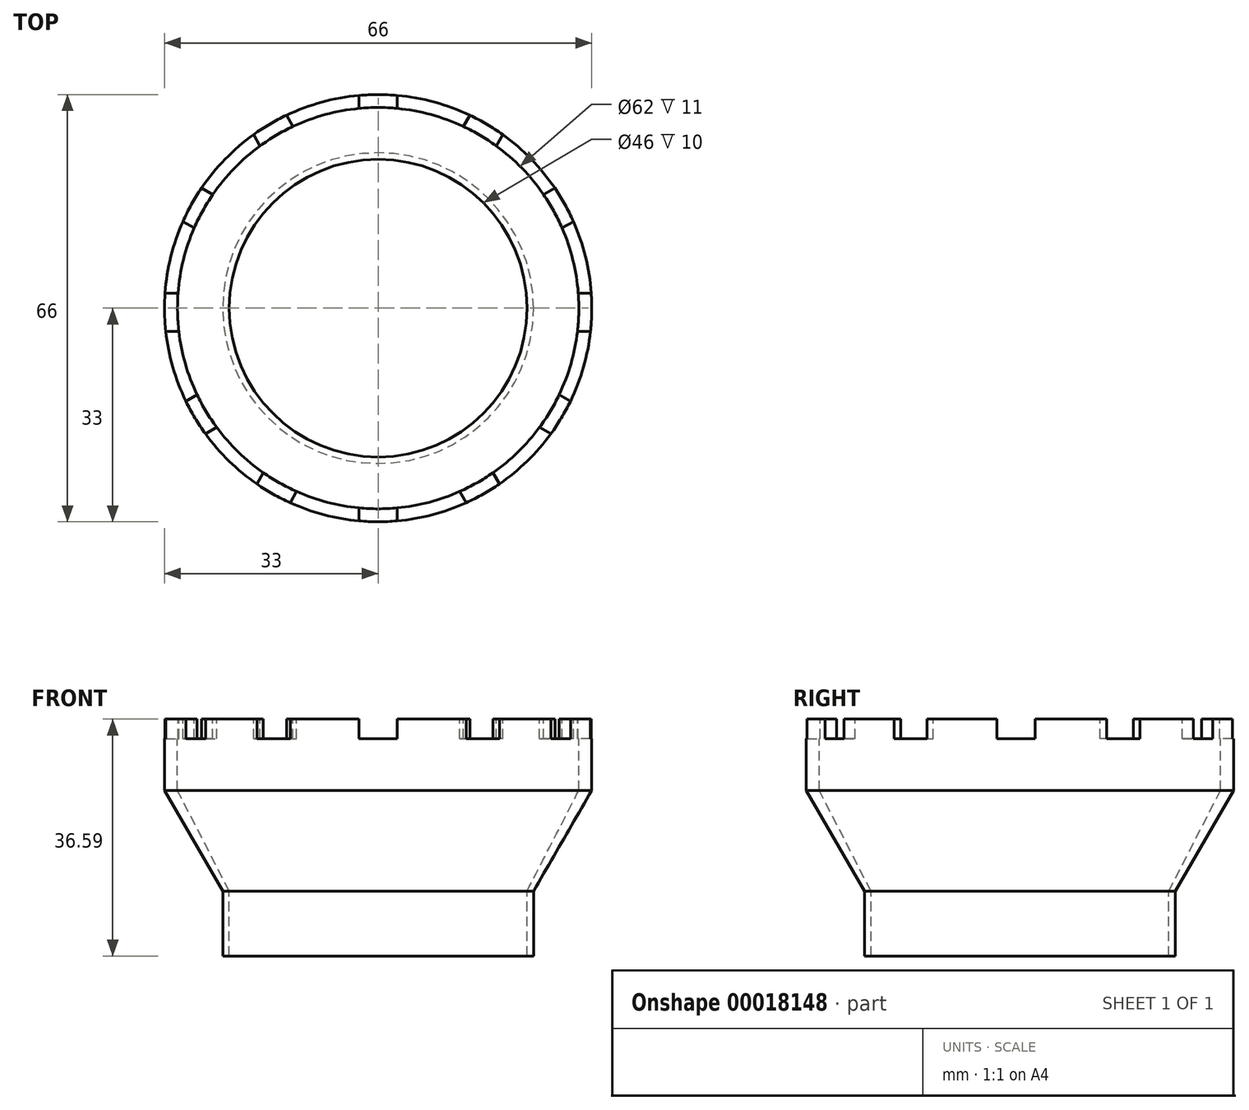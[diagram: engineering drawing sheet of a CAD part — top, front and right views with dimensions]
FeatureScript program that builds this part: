
annotation { "Feature Type Name" : "Feature", "Feature Type Description" : "" }
export const myFeature = defineFeature(function(context is Context, id is Id, definition is map)
    precondition{}
    {
        {
            var Q0;
            Q0=qCreatedBy(makeId("Top.planeOp"),FACE);
            var sketch = newSketch(context, id + "F0", { "sketchPlane" : qUnion([Q0])});
            skCircle(sketch, "E0", {"center": v(0, 0) * mm, "radius": 24 * mm});
            skSolve(sketch);
        }
        {
            var Q0;
            Q0=makeQuery(id+"F0.imprint","IMPRINT",FACE,{"disambiguationData":[TD([[makeQuery(id+"F0.imprint","IMPRINT",EDGE,{"derivedFrom":sQuery(id+"F0.wireOp",EDGE,"E0")}),1.0]])]});
            extrude(context, id + "F1", {"entities" : qUnion([Q0]), "depth" : 10 * mm});
        }
        {
            var Q0;
            Q0=makeQuery(id+"F1.opExtrude","CAP_FACE",FACE,{"disambiguationData":[OSD([sQuery(id+"F0.wireOp",EDGE,"E0")])],"isStart":false});
            var sketch = newSketch(context, id + "F2", { "sketchPlane" : qUnion([Q0])});
            skCircle(sketch, "E1", {"center": v(0, 0) * mm, "radius": 23 * mm});
            skSolve(sketch);
        }
        {
            var Q0;
            Q0=qSketchRegion(id+"F2",true);
            extrude(context, id + "F3", {"entities" : qUnion([Q0]), "operationType" : NewBodyOperationType.REMOVE, "endBound" : BoundingType.THROUGH_ALL, "oppositeDirection" : true, "depth" : 25 * mm});
        }
        {
            var Q0;
            Q0=qCreatedBy(makeId("Front.planeOp"),FACE);
            var sketch = newSketch(context, id + "F4", { "sketchPlane" : qUnion([Q0])});
            skLineSegment(sketch, "E2", {"start": v(-31, 25.59) * mm, "end": v(-31, 36.59) * mm});
            skLineSegment(sketch, "E3", {"start": v(-31, 36.59) * mm, "end": v(-33, 36.59) * mm});
            skLineSegment(sketch, "E4", {"start": v(-33, 36.59) * mm, "end": v(-33, 25.59) * mm});
            skLineSegment(sketch, "E5", {"start": v(-33, 25.59) * mm, "end": v(-24, 10) * mm});
            skLineSegment(sketch, "E6", {"start": v(-24, 10) * mm, "end": v(-23, 10) * mm});
            skLineSegment(sketch, "E7", {"start": v(-23, 10) * mm, "end": v(-31, 25.59) * mm});
            skLineSegment(sketch, "E8.0", {"start": v(-24, 10) * mm, "end": v(24, 10) * mm});
            skLineSegment(sketch, "E9", {"start": v(-33, 25.59) * mm, "end": v(-33, 10) * mm, "construction": true});
            skSolve(sketch);
        }
        {
            var Q0;
            Q0=qSketchRegion(id+"F4",true);
            var Q1;
            Q1=makeQuery(id+"F3.boolean.opBoolean","COPY",FACE,{"derivedFrom":makeQuery(id+"F3.opExtrude","SWEPT_FACE",FACE,{"disambiguationData":[OSD([sQuery(id+"F2.wireOp",EDGE,"E1")])]})});
            revolve(context, id + "F5", {"operationType" : NewBodyOperationType.ADD, "entities" : qUnion([Q0]), "axis" : qUnion([Q1]), "revolveType" : RevolveType.FULL});
        }
        {
            var Q0;
            Q0=makeQuery(id+"F5.opRevolve","SWEPT_FACE",FACE,{"disambiguationData":[OSD([sQuery(id+"F4.wireOp",EDGE,"E3")])]});
            var sketch = newSketch(context, id + "F6", { "sketchPlane" : qUnion([Q0])});
            skLineSegment(sketch, "E10.rect.bottom", {"start": v(-2.95, 33.18) * mm, "end": v(2.95, 33.18) * mm});
            skLineSegment(sketch, "E10.rect.top", {"start": v(-2.95, 28.82) * mm, "end": v(2.95, 28.82) * mm});
            skLineSegment(sketch, "E10.rect.left", {"start": v(-2.95, 33.18) * mm, "end": v(-2.95, 28.82) * mm});
            skLineSegment(sketch, "E10.rect.right", {"start": v(2.95, 33.18) * mm, "end": v(2.95, 28.82) * mm});
            skPoint(sketch, "E10.rect.middle", {"position": v(0, 31) * mm});
            skPoint(sketch, "E11.1.2", {"position": v(-15.8, 26.76) * mm});
            skLineSegment(sketch, "E11.1.9", {"start": v(-19.46, 27.18) * mm, "end": v(-14.35, 30.13) * mm});
            skLineSegment(sketch, "E11.1.10", {"start": v(-17.27, 23.4) * mm, "end": v(-12.16, 26.35) * mm});
            skLineSegment(sketch, "E11.1.11", {"start": v(-19.46, 27.18) * mm, "end": v(-17.27, 23.4) * mm});
            skLineSegment(sketch, "E11.1.12", {"start": v(-14.35, 30.13) * mm, "end": v(-12.16, 26.35) * mm});
            skPoint(sketch, "E11.2.2", {"position": v(-27.38, 15.2) * mm});
            skLineSegment(sketch, "E11.2.9", {"start": v(-30.75, 13.73) * mm, "end": v(-27.8, 18.84) * mm});
            skLineSegment(sketch, "E11.2.10", {"start": v(-26.97, 11.54) * mm, "end": v(-24.02, 16.65) * mm});
            skLineSegment(sketch, "E11.2.11", {"start": v(-30.75, 13.73) * mm, "end": v(-26.97, 11.54) * mm});
            skLineSegment(sketch, "E11.2.12", {"start": v(-27.8, 18.84) * mm, "end": v(-24.02, 16.65) * mm});
            skPoint(sketch, "E11.3.2", {"position": v(-31.62, -0.62) * mm});
            skLineSegment(sketch, "E11.3.9", {"start": v(-33.8, -3.57) * mm, "end": v(-33.8, 2.33) * mm});
            skLineSegment(sketch, "E11.3.10", {"start": v(-29.43, -3.57) * mm, "end": v(-29.43, 2.33) * mm});
            skLineSegment(sketch, "E11.3.11", {"start": v(-33.8, -3.57) * mm, "end": v(-29.43, -3.57) * mm});
            skLineSegment(sketch, "E11.3.12", {"start": v(-33.8, 2.33) * mm, "end": v(-29.43, 2.33) * mm});
            skPoint(sketch, "E11.4.2", {"position": v(-27.38, -16.43) * mm});
            skLineSegment(sketch, "E11.4.9", {"start": v(-27.8, -20.07) * mm, "end": v(-30.75, -14.97) * mm});
            skLineSegment(sketch, "E11.4.10", {"start": v(-24.02, -17.89) * mm, "end": v(-26.97, -12.78) * mm});
            skLineSegment(sketch, "E11.4.11", {"start": v(-27.8, -20.07) * mm, "end": v(-24.02, -17.89) * mm});
            skLineSegment(sketch, "E11.4.12", {"start": v(-30.75, -14.97) * mm, "end": v(-26.97, -12.78) * mm});
            skPoint(sketch, "E11.5.2", {"position": v(-15.8, -28) * mm});
            skLineSegment(sketch, "E11.5.9", {"start": v(-14.35, -31.37) * mm, "end": v(-19.46, -28.42) * mm});
            skLineSegment(sketch, "E11.5.10", {"start": v(-12.16, -27.58) * mm, "end": v(-17.27, -24.63) * mm});
            skLineSegment(sketch, "E11.5.11", {"start": v(-14.35, -31.37) * mm, "end": v(-12.16, -27.58) * mm});
            skLineSegment(sketch, "E11.5.12", {"start": v(-19.46, -28.42) * mm, "end": v(-17.27, -24.63) * mm});
            skPoint(sketch, "E11.6.2", {"position": v(0, -32.24) * mm});
            skLineSegment(sketch, "E11.6.9", {"start": v(2.95, -34.42) * mm, "end": v(-2.95, -34.42) * mm});
            skLineSegment(sketch, "E11.6.10", {"start": v(2.95, -30.05) * mm, "end": v(-2.95, -30.05) * mm});
            skLineSegment(sketch, "E11.6.11", {"start": v(2.95, -34.42) * mm, "end": v(2.95, -30.05) * mm});
            skLineSegment(sketch, "E11.6.12", {"start": v(-2.95, -34.42) * mm, "end": v(-2.95, -30.05) * mm});
            skPoint(sketch, "E11.7.2", {"position": v(15.8, -28) * mm});
            skLineSegment(sketch, "E11.7.9", {"start": v(19.46, -28.42) * mm, "end": v(14.35, -31.37) * mm});
            skLineSegment(sketch, "E11.7.10", {"start": v(17.27, -24.63) * mm, "end": v(12.16, -27.58) * mm});
            skLineSegment(sketch, "E11.7.11", {"start": v(19.46, -28.42) * mm, "end": v(17.27, -24.63) * mm});
            skLineSegment(sketch, "E11.7.12", {"start": v(14.35, -31.37) * mm, "end": v(12.16, -27.58) * mm});
            skPoint(sketch, "E11.center", {"position": v(0, -0.62) * mm});
            skPoint(sketch, "E12.2.8.0", {"position": v(27.38, -16.43) * mm});
            skLineSegment(sketch, "E12.9.8.0", {"start": v(30.75, -14.97) * mm, "end": v(27.8, -20.07) * mm});
            skLineSegment(sketch, "E12.12.8.0", {"start": v(26.97, -12.78) * mm, "end": v(24.02, -17.89) * mm});
            skLineSegment(sketch, "E12.15.8.0", {"start": v(30.75, -14.97) * mm, "end": v(26.97, -12.78) * mm});
            skLineSegment(sketch, "E12.18.8.0", {"start": v(27.8, -20.07) * mm, "end": v(24.02, -17.89) * mm});
            skPoint(sketch, "E12.2.9.0", {"position": v(31.62, -0.62) * mm});
            skLineSegment(sketch, "E12.9.9.0", {"start": v(33.8, 2.33) * mm, "end": v(33.8, -3.57) * mm});
            skLineSegment(sketch, "E12.12.9.0", {"start": v(29.43, 2.33) * mm, "end": v(29.43, -3.57) * mm});
            skLineSegment(sketch, "E12.15.9.0", {"start": v(33.8, 2.33) * mm, "end": v(29.43, 2.33) * mm});
            skLineSegment(sketch, "E12.18.9.0", {"start": v(33.8, -3.57) * mm, "end": v(29.43, -3.57) * mm});
            skPoint(sketch, "E12.2.10.0", {"position": v(27.38, 15.2) * mm});
            skLineSegment(sketch, "E12.9.10.0", {"start": v(27.8, 18.84) * mm, "end": v(30.75, 13.73) * mm});
            skLineSegment(sketch, "E12.12.10.0", {"start": v(24.02, 16.65) * mm, "end": v(26.97, 11.54) * mm});
            skLineSegment(sketch, "E12.15.10.0", {"start": v(27.8, 18.84) * mm, "end": v(24.02, 16.65) * mm});
            skLineSegment(sketch, "E12.18.10.0", {"start": v(30.75, 13.73) * mm, "end": v(26.97, 11.54) * mm});
            skPoint(sketch, "E12.2.11.0", {"position": v(15.8, 26.76) * mm});
            skLineSegment(sketch, "E12.9.11.0", {"start": v(14.35, 30.13) * mm, "end": v(19.46, 27.18) * mm});
            skLineSegment(sketch, "E12.12.11.0", {"start": v(12.16, 26.35) * mm, "end": v(17.27, 23.4) * mm});
            skLineSegment(sketch, "E12.15.11.0", {"start": v(14.35, 30.13) * mm, "end": v(12.16, 26.35) * mm});
            skLineSegment(sketch, "E12.18.11.0", {"start": v(19.46, 27.18) * mm, "end": v(17.27, 23.4) * mm});
            skSolve(sketch);
        }
        {
            var Q0;
            Q0 = qSketchRegion(id + "F6", true);
            extrude(context, id + "F7", {"entities" : qUnion([Q0]), "operationType" : NewBodyOperationType.REMOVE, "oppositeDirection" : true, "depth" : 3 * mm});
        }
    });
